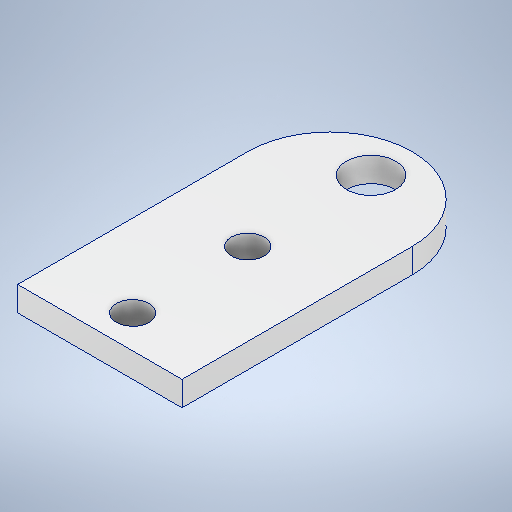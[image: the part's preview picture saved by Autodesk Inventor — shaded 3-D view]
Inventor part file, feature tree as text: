
AUTODESK INVENTOR PART (.ipt)
format: ipt  version: 2025 (Build 290162000, 162)  size: 259,072 bytes
history: native  units: mm
features: sketch x3, hole x2, projected_geometry x2, other x1, extrude x1
ambient origin geometry x8: Origin, YZ Plane, XZ Plane, XY Plane, X Axis, Y Axis, Z Axis, Center Point
bodies: Body1 (feature_tree)
feature tree (9):
  other  "Těleso1"
  extrude  "Vysunutí1"  Depth=5.0mm
  hole  "Díra1"  [1 undecoded]
  hole  "Díra2"  [1 undecoded]
  sketch  "Náčrt1"
  sketch  "Náčrt2"
  projected_geometry  "Promítnutá smyčka1"
  sketch  "Náčrt3"
  projected_geometry  "Promítnutá smyčka2"
note: 2 required parameter values undecoded (feature->parameter linkage not recoverable at this tier; creation-order binding heuristic only, values carry confidence <= 0.55)
